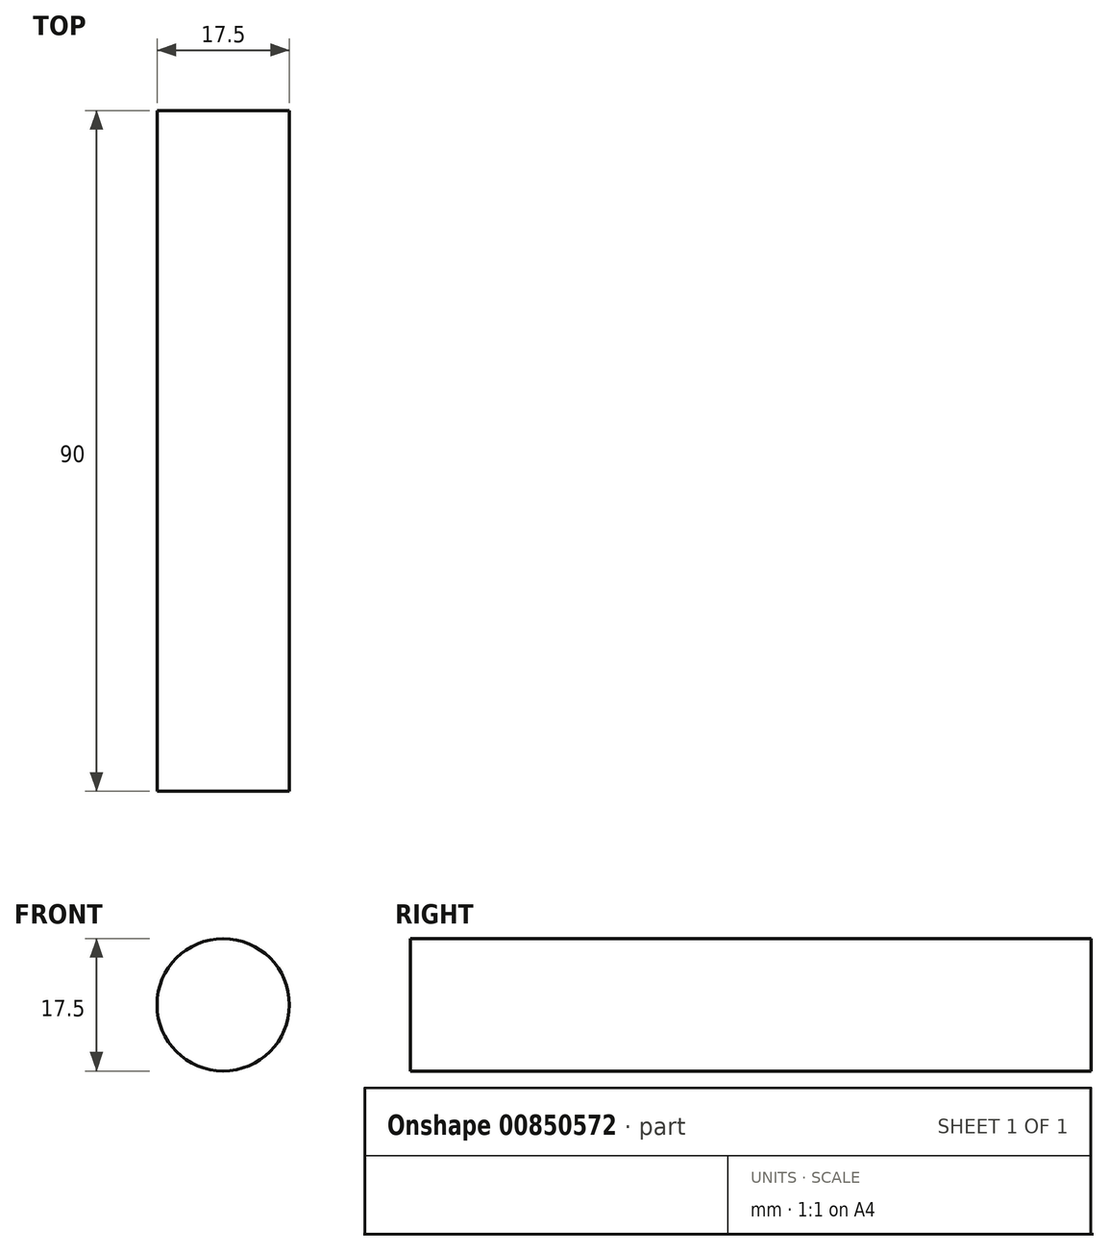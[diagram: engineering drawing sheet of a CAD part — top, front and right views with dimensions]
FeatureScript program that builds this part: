
annotation { "Feature Type Name" : "Feature", "Feature Type Description" : "" }
export const myFeature = defineFeature(function(context is Context, id is Id, definition is map)
    precondition{}
    {
        {
            var Q0;
            Q0=qCreatedBy(makeId("Front.planeOp"),FACE);
            var sketch = newSketch(context, id + "F0", { "sketchPlane" : qUnion([Q0])});
            skCircle(sketch, "E0", {"center": v(0, 0) * mm, "radius": 8.75 * mm});
            skSolve(sketch);
        }
        {
            var Q0;
            Q0 = qSketchRegion(id + "F0", true);
            extrude(context, id + "F1", {"entities" : qUnion([Q0]), "depth" : 90 * mm, "offsetDistance" : 25 * mm});
        }
    });
